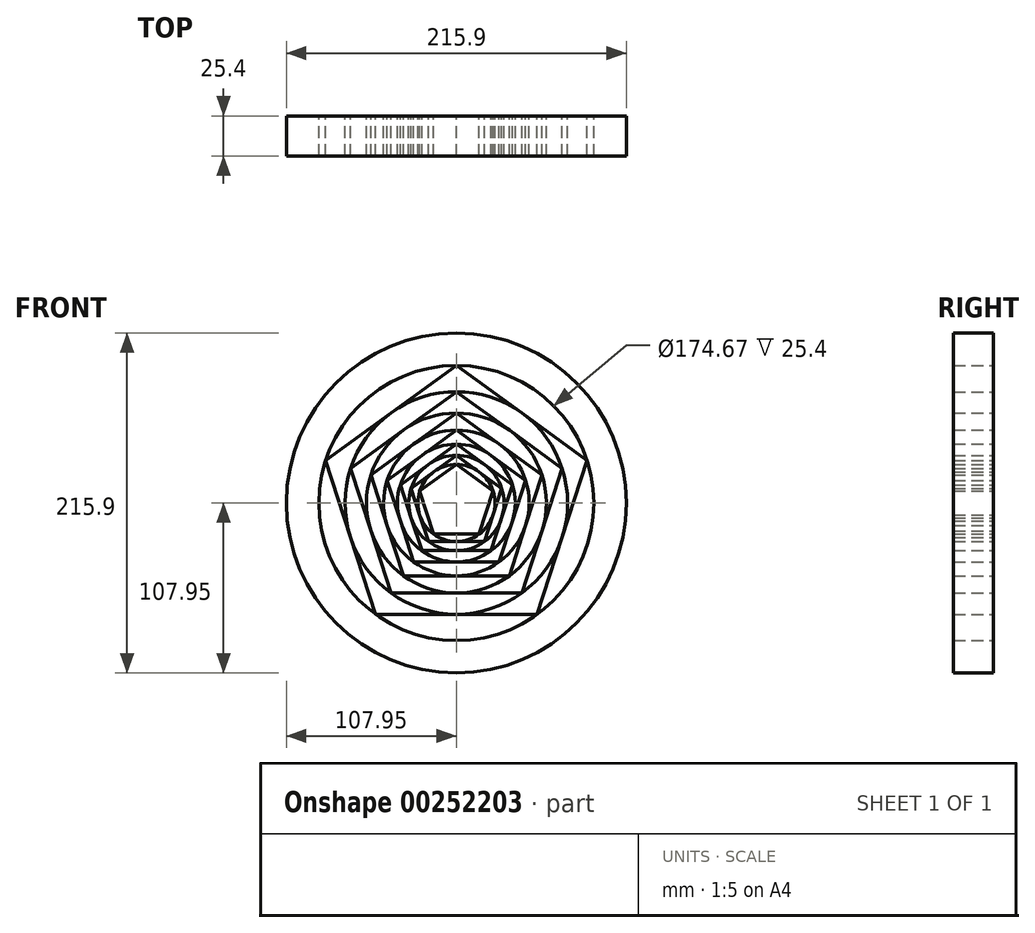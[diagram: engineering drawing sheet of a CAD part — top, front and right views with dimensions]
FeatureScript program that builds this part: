
annotation { "Feature Type Name" : "Feature", "Feature Type Description" : "" }
export const myFeature = defineFeature(function(context is Context, id is Id, definition is map)
    precondition{}
    {
        {
            var Q0;
            Q0=qCreatedBy(makeId("Front.planeOp"),FACE);
            var sketch = newSketch(context, id + "F0", { "sketchPlane" : qUnion([Q0])});
            skCircle(sketch, "E0", {"center": v(0, 0) * mm, "radius": 107.95 * mm});
            skCircle(sketch, "E1.cCircle", {"center": v(0, 0) * mm, "radius": 107.95 * mm, "construction": true});
            skLineSegment(sketch, "E2.0", {"start": v(-2.52, 107.92) * mm, "end": v(101.86, 35.74) * mm});
            skLineSegment(sketch, "E2.1", {"start": v(101.86, 35.74) * mm, "end": v(65.47, -85.83) * mm});
            skLineSegment(sketch, "E2.2", {"start": v(65.47, -85.83) * mm, "end": v(-61.4, -88.79) * mm});
            skLineSegment(sketch, "E2.3", {"start": v(-61.4, -88.79) * mm, "end": v(-103.42, 30.96) * mm});
            skLineSegment(sketch, "E2.4", {"start": v(-103.42, 30.96) * mm, "end": v(-2.52, 107.92) * mm});
            skCircle(sketch, "E3", {"center": v(0, 0) * mm, "radius": 87.33 * mm});
            skCircle(sketch, "E4.cCircle", {"center": v(0, 0) * mm, "radius": 87.33 * mm, "construction": true});
            skLineSegment(sketch, "E4.0", {"start": v(0, 87.33) * mm, "end": v(83.06, 26.99) * mm});
            skLineSegment(sketch, "E4.1", {"start": v(83.06, 26.99) * mm, "end": v(51.33, -70.65) * mm});
            skLineSegment(sketch, "E4.2", {"start": v(51.33, -70.65) * mm, "end": v(-51.33, -70.65) * mm});
            skLineSegment(sketch, "E4.3", {"start": v(-51.33, -70.65) * mm, "end": v(-83.06, 26.99) * mm});
            skLineSegment(sketch, "E4.4", {"start": v(-83.06, 26.99) * mm, "end": v(0, 87.33) * mm});
            skCircle(sketch, "E5", {"center": v(0, 0) * mm, "radius": 70.65 * mm});
            skCircle(sketch, "E6.cCircle", {"center": v(0, 0) * mm, "radius": 70.65 * mm, "construction": true});
            skLineSegment(sketch, "E6.0", {"start": v(0, 70.65) * mm, "end": v(67.2, 21.83) * mm});
            skLineSegment(sketch, "E6.1", {"start": v(67.2, 21.83) * mm, "end": v(41.53, -57.16) * mm});
            skLineSegment(sketch, "E6.2", {"start": v(41.53, -57.16) * mm, "end": v(-41.53, -57.16) * mm});
            skLineSegment(sketch, "E6.3", {"start": v(-41.53, -57.16) * mm, "end": v(-67.2, 21.83) * mm});
            skLineSegment(sketch, "E6.4", {"start": v(-67.2, 21.83) * mm, "end": v(0, 70.65) * mm});
            skCircle(sketch, "E7", {"center": v(0, 0) * mm, "radius": 57.16 * mm});
            skCircle(sketch, "E8.cCircle", {"center": v(0, 0) * mm, "radius": 57.16 * mm, "construction": true});
            skLineSegment(sketch, "E8.0", {"start": v(0, 57.16) * mm, "end": v(54.36, 17.66) * mm});
            skLineSegment(sketch, "E8.1", {"start": v(54.36, 17.66) * mm, "end": v(33.6, -46.24) * mm});
            skLineSegment(sketch, "E8.2", {"start": v(33.6, -46.24) * mm, "end": v(-33.6, -46.24) * mm});
            skLineSegment(sketch, "E8.3", {"start": v(-33.6, -46.24) * mm, "end": v(-54.36, 17.66) * mm});
            skLineSegment(sketch, "E8.4", {"start": v(-54.36, 17.66) * mm, "end": v(0, 57.16) * mm});
            skCircle(sketch, "E9", {"center": v(0, 0) * mm, "radius": 46.24 * mm});
            skCircle(sketch, "E10.cCircle", {"center": v(0, 0) * mm, "radius": 46.24 * mm, "construction": true});
            skLineSegment(sketch, "E10.0", {"start": v(0, 46.24) * mm, "end": v(43.98, 14.3) * mm});
            skLineSegment(sketch, "E10.1", {"start": v(43.98, 14.3) * mm, "end": v(27.18, -37.41) * mm});
            skLineSegment(sketch, "E10.2", {"start": v(27.18, -37.41) * mm, "end": v(-27.18, -37.41) * mm});
            skLineSegment(sketch, "E10.3", {"start": v(-27.18, -37.41) * mm, "end": v(-43.98, 14.3) * mm});
            skLineSegment(sketch, "E10.4", {"start": v(-43.98, 14.3) * mm, "end": v(0, 46.24) * mm});
            skCircle(sketch, "E11", {"center": v(0, 0) * mm, "radius": 37.41 * mm});
            skCircle(sketch, "E12.cCircle", {"center": v(0, 0) * mm, "radius": 37.41 * mm, "construction": true});
            skLineSegment(sketch, "E12.0", {"start": v(0, 37.41) * mm, "end": v(35.58, 11.56) * mm});
            skLineSegment(sketch, "E12.1", {"start": v(35.58, 11.56) * mm, "end": v(22, -30.27) * mm});
            skLineSegment(sketch, "E12.2", {"start": v(22, -30.27) * mm, "end": v(-22, -30.27) * mm});
            skLineSegment(sketch, "E12.3", {"start": v(-22, -30.27) * mm, "end": v(-35.58, 11.56) * mm});
            skLineSegment(sketch, "E12.4", {"start": v(-35.58, 11.56) * mm, "end": v(0, 37.41) * mm});
            skCircle(sketch, "E13", {"center": v(0, 0) * mm, "radius": 30.27 * mm});
            skCircle(sketch, "E14.cCircle", {"center": v(0, 0) * mm, "radius": 30.27 * mm, "construction": true});
            skLineSegment(sketch, "E14.0", {"start": v(0, 30.27) * mm, "end": v(28.79, 9.35) * mm});
            skLineSegment(sketch, "E14.1", {"start": v(28.79, 9.35) * mm, "end": v(17.8, -24.49) * mm});
            skLineSegment(sketch, "E14.2", {"start": v(17.8, -24.49) * mm, "end": v(-17.8, -24.49) * mm});
            skLineSegment(sketch, "E14.3", {"start": v(-17.8, -24.49) * mm, "end": v(-28.79, 9.35) * mm});
            skLineSegment(sketch, "E14.4", {"start": v(-28.79, 9.35) * mm, "end": v(0, 30.27) * mm});
            skCircle(sketch, "E15", {"center": v(0, 0) * mm, "radius": 24.49 * mm});
            skCircle(sketch, "E16.cCircle", {"center": v(0, 0) * mm, "radius": 24.49 * mm, "construction": true});
            skLineSegment(sketch, "E16.0", {"start": v(0, 24.49) * mm, "end": v(23.29, 7.57) * mm});
            skLineSegment(sketch, "E16.1", {"start": v(23.29, 7.57) * mm, "end": v(14.4, -19.8) * mm});
            skLineSegment(sketch, "E16.2", {"start": v(14.4, -19.8) * mm, "end": v(-14.4, -19.8) * mm});
            skLineSegment(sketch, "E16.3", {"start": v(-14.4, -19.8) * mm, "end": v(-23.29, 7.57) * mm});
            skLineSegment(sketch, "E16.4", {"start": v(-23.29, 7.57) * mm, "end": v(0, 24.49) * mm});
            skSolve(sketch);
        }
        {
            var Q0;
            Q0 = qSketchRegion(id + "F0", true);
            var Q1;
            Q1=makeQuery(id+"F0.imprint","IMPRINT",FACE,{"disambiguationData":[TD([[makeQuery(id+"F0.imprint","IMPRINT",EDGE,{"derivedFrom":sQuery(id+"F0.wireOp",EDGE,"E16.0")}),-1.0]])]});
            var Q2;
            {var subQ1=sQuery(id+"F0.wireOp",EDGE,"E14.3");var subQ3=sQuery(id+"F0.wireOp",EDGE,"E15");var subQ4=makeQuery(id+"F0.imprint","INTERSECT",VERTEX,{"derivedFrom":[subQ1,subQ3]});Q2=makeQuery(id+"F0.imprint","IMPRINT",FACE,{"disambiguationData":[TD([[makeQuery(id+"F0.imprint","IMPRINT",EDGE,{"disambiguationData":[TD([[subQ4,-1.0]])],"derivedFrom":subQ1}),-1.0]])]});}
            var Q3;
            {var subQ1=sQuery(id+"F0.wireOp",EDGE,"E14.2");var subQ3=sQuery(id+"F0.wireOp",EDGE,"E15");var subQ4=makeQuery(id+"F0.imprint","INTERSECT",VERTEX,{"derivedFrom":[subQ1,subQ3]});Q3=makeQuery(id+"F0.imprint","IMPRINT",FACE,{"disambiguationData":[TD([[makeQuery(id+"F0.imprint","IMPRINT",EDGE,{"disambiguationData":[TD([[subQ4,-1.0]])],"derivedFrom":subQ1}),-1.0]])]});}
            var Q4;
            {var subQ1=sQuery(id+"F0.wireOp",EDGE,"E14.1");var subQ3=sQuery(id+"F0.wireOp",EDGE,"E15");var subQ4=makeQuery(id+"F0.imprint","INTERSECT",VERTEX,{"derivedFrom":[subQ1,subQ3]});Q4=makeQuery(id+"F0.imprint","IMPRINT",FACE,{"disambiguationData":[TD([[makeQuery(id+"F0.imprint","IMPRINT",EDGE,{"disambiguationData":[TD([[subQ4,-1.0]])],"derivedFrom":subQ1}),-1.0]])]});}
            var Q5;
            {var subQ1=sQuery(id+"F0.wireOp",EDGE,"E14.0");var subQ3=sQuery(id+"F0.wireOp",EDGE,"E15");var subQ4=makeQuery(id+"F0.imprint","INTERSECT",VERTEX,{"derivedFrom":[subQ1,subQ3]});Q5=makeQuery(id+"F0.imprint","IMPRINT",FACE,{"disambiguationData":[TD([[makeQuery(id+"F0.imprint","IMPRINT",EDGE,{"disambiguationData":[TD([[subQ4,-1.0]])],"derivedFrom":subQ1}),-1.0]])]});}
            var Q6;
            {var subQ1=sQuery(id+"F0.wireOp",EDGE,"E14.0");var subQ3=sQuery(id+"F0.wireOp",EDGE,"E15");var subQ4=makeQuery(id+"F0.imprint","INTERSECT",VERTEX,{"derivedFrom":[subQ1,subQ3]});Q6=makeQuery(id+"F0.imprint","IMPRINT",FACE,{"disambiguationData":[TD([[makeQuery(id+"F0.imprint","IMPRINT",EDGE,{"disambiguationData":[TD([[subQ4,1.0]])],"derivedFrom":subQ1}),-1.0]])]});}
            var Q7;
            {var subQ1=sQuery(id+"F0.wireOp",EDGE,"E12.0");var subQ3=sQuery(id+"F0.wireOp",EDGE,"E13");var subQ4=makeQuery(id+"F0.imprint","INTERSECT",VERTEX,{"derivedFrom":[subQ1,subQ3]});Q7=makeQuery(id+"F0.imprint","IMPRINT",FACE,{"disambiguationData":[TD([[makeQuery(id+"F0.imprint","IMPRINT",EDGE,{"disambiguationData":[TD([[subQ4,1.0]])],"derivedFrom":subQ1}),-1.0]])]});}
            var Q8;
            {var subQ1=sQuery(id+"F0.wireOp",EDGE,"E12.3");var subQ3=sQuery(id+"F0.wireOp",EDGE,"E13");var subQ4=makeQuery(id+"F0.imprint","INTERSECT",VERTEX,{"derivedFrom":[subQ1,subQ3]});Q8=makeQuery(id+"F0.imprint","IMPRINT",FACE,{"disambiguationData":[TD([[makeQuery(id+"F0.imprint","IMPRINT",EDGE,{"disambiguationData":[TD([[subQ4,-1.0]])],"derivedFrom":subQ1}),-1.0]])]});}
            var Q9;
            {var subQ1=sQuery(id+"F0.wireOp",EDGE,"E12.2");var subQ3=sQuery(id+"F0.wireOp",EDGE,"E13");var subQ4=makeQuery(id+"F0.imprint","INTERSECT",VERTEX,{"derivedFrom":[subQ1,subQ3]});Q9=makeQuery(id+"F0.imprint","IMPRINT",FACE,{"disambiguationData":[TD([[makeQuery(id+"F0.imprint","IMPRINT",EDGE,{"disambiguationData":[TD([[subQ4,-1.0]])],"derivedFrom":subQ1}),-1.0]])]});}
            var Q10;
            {var subQ1=sQuery(id+"F0.wireOp",EDGE,"E12.1");var subQ3=sQuery(id+"F0.wireOp",EDGE,"E13");var subQ4=makeQuery(id+"F0.imprint","INTERSECT",VERTEX,{"derivedFrom":[subQ1,subQ3]});Q10=makeQuery(id+"F0.imprint","IMPRINT",FACE,{"disambiguationData":[TD([[makeQuery(id+"F0.imprint","IMPRINT",EDGE,{"disambiguationData":[TD([[subQ4,-1.0]])],"derivedFrom":subQ1}),-1.0]])]});}
            var Q11;
            {var subQ1=sQuery(id+"F0.wireOp",EDGE,"E12.0");var subQ3=sQuery(id+"F0.wireOp",EDGE,"E13");var subQ4=makeQuery(id+"F0.imprint","INTERSECT",VERTEX,{"derivedFrom":[subQ1,subQ3]});Q11=makeQuery(id+"F0.imprint","IMPRINT",FACE,{"disambiguationData":[TD([[makeQuery(id+"F0.imprint","IMPRINT",EDGE,{"disambiguationData":[TD([[subQ4,-1.0]])],"derivedFrom":subQ1}),-1.0]])]});}
            var Q12;
            {var subQ1=sQuery(id+"F0.wireOp",EDGE,"E10.0");var subQ3=sQuery(id+"F0.wireOp",EDGE,"E11");var subQ4=makeQuery(id+"F0.imprint","INTERSECT",VERTEX,{"derivedFrom":[subQ1,subQ3]});Q12=makeQuery(id+"F0.imprint","IMPRINT",FACE,{"disambiguationData":[TD([[makeQuery(id+"F0.imprint","IMPRINT",EDGE,{"disambiguationData":[TD([[subQ4,1.0]])],"derivedFrom":subQ1}),-1.0]])]});}
            var Q13;
            {var subQ1=sQuery(id+"F0.wireOp",EDGE,"E10.3");var subQ3=sQuery(id+"F0.wireOp",EDGE,"E11");var subQ4=makeQuery(id+"F0.imprint","INTERSECT",VERTEX,{"derivedFrom":[subQ1,subQ3]});Q13=makeQuery(id+"F0.imprint","IMPRINT",FACE,{"disambiguationData":[TD([[makeQuery(id+"F0.imprint","IMPRINT",EDGE,{"disambiguationData":[TD([[subQ4,-1.0]])],"derivedFrom":subQ1}),-1.0]])]});}
            var Q14;
            {var subQ1=sQuery(id+"F0.wireOp",EDGE,"E10.2");var subQ3=sQuery(id+"F0.wireOp",EDGE,"E11");var subQ4=makeQuery(id+"F0.imprint","INTERSECT",VERTEX,{"derivedFrom":[subQ1,subQ3]});Q14=makeQuery(id+"F0.imprint","IMPRINT",FACE,{"disambiguationData":[TD([[makeQuery(id+"F0.imprint","IMPRINT",EDGE,{"disambiguationData":[TD([[subQ4,-1.0]])],"derivedFrom":subQ1}),-1.0]])]});}
            var Q15;
            {var subQ1=sQuery(id+"F0.wireOp",EDGE,"E10.1");var subQ3=sQuery(id+"F0.wireOp",EDGE,"E11");var subQ4=makeQuery(id+"F0.imprint","INTERSECT",VERTEX,{"derivedFrom":[subQ1,subQ3]});Q15=makeQuery(id+"F0.imprint","IMPRINT",FACE,{"disambiguationData":[TD([[makeQuery(id+"F0.imprint","IMPRINT",EDGE,{"disambiguationData":[TD([[subQ4,-1.0]])],"derivedFrom":subQ1}),-1.0]])]});}
            var Q16;
            {var subQ1=sQuery(id+"F0.wireOp",EDGE,"E10.0");var subQ3=sQuery(id+"F0.wireOp",EDGE,"E11");var subQ4=makeQuery(id+"F0.imprint","INTERSECT",VERTEX,{"derivedFrom":[subQ1,subQ3]});Q16=makeQuery(id+"F0.imprint","IMPRINT",FACE,{"disambiguationData":[TD([[makeQuery(id+"F0.imprint","IMPRINT",EDGE,{"disambiguationData":[TD([[subQ4,-1.0]])],"derivedFrom":subQ1}),-1.0]])]});}
            var Q17;
            {var subQ1=sQuery(id+"F0.wireOp",EDGE,"E8.0");var subQ3=sQuery(id+"F0.wireOp",EDGE,"E9");var subQ4=makeQuery(id+"F0.imprint","INTERSECT",VERTEX,{"derivedFrom":[subQ1,subQ3]});Q17=makeQuery(id+"F0.imprint","IMPRINT",FACE,{"disambiguationData":[TD([[makeQuery(id+"F0.imprint","IMPRINT",EDGE,{"disambiguationData":[TD([[subQ4,1.0]])],"derivedFrom":subQ1}),-1.0]])]});}
            var Q18;
            {var subQ1=sQuery(id+"F0.wireOp",EDGE,"E8.3");var subQ3=sQuery(id+"F0.wireOp",EDGE,"E9");var subQ4=makeQuery(id+"F0.imprint","INTERSECT",VERTEX,{"derivedFrom":[subQ1,subQ3]});Q18=makeQuery(id+"F0.imprint","IMPRINT",FACE,{"disambiguationData":[TD([[makeQuery(id+"F0.imprint","IMPRINT",EDGE,{"disambiguationData":[TD([[subQ4,-1.0]])],"derivedFrom":subQ1}),-1.0]])]});}
            var Q19;
            {var subQ1=sQuery(id+"F0.wireOp",EDGE,"E8.2");var subQ3=sQuery(id+"F0.wireOp",EDGE,"E9");var subQ4=makeQuery(id+"F0.imprint","INTERSECT",VERTEX,{"derivedFrom":[subQ1,subQ3]});Q19=makeQuery(id+"F0.imprint","IMPRINT",FACE,{"disambiguationData":[TD([[makeQuery(id+"F0.imprint","IMPRINT",EDGE,{"disambiguationData":[TD([[subQ4,-1.0]])],"derivedFrom":subQ1}),-1.0]])]});}
            var Q20;
            {var subQ1=sQuery(id+"F0.wireOp",EDGE,"E8.1");var subQ3=sQuery(id+"F0.wireOp",EDGE,"E9");var subQ4=makeQuery(id+"F0.imprint","INTERSECT",VERTEX,{"derivedFrom":[subQ1,subQ3]});Q20=makeQuery(id+"F0.imprint","IMPRINT",FACE,{"disambiguationData":[TD([[makeQuery(id+"F0.imprint","IMPRINT",EDGE,{"disambiguationData":[TD([[subQ4,-1.0]])],"derivedFrom":subQ1}),-1.0]])]});}
            var Q21;
            {var subQ1=sQuery(id+"F0.wireOp",EDGE,"E8.0");var subQ3=sQuery(id+"F0.wireOp",EDGE,"E9");var subQ4=makeQuery(id+"F0.imprint","INTERSECT",VERTEX,{"derivedFrom":[subQ1,subQ3]});Q21=makeQuery(id+"F0.imprint","IMPRINT",FACE,{"disambiguationData":[TD([[makeQuery(id+"F0.imprint","IMPRINT",EDGE,{"disambiguationData":[TD([[subQ4,-1.0]])],"derivedFrom":subQ1}),-1.0]])]});}
            var Q22;
            {var subQ1=sQuery(id+"F0.wireOp",EDGE,"E6.0");var subQ3=sQuery(id+"F0.wireOp",EDGE,"E7");var subQ4=makeQuery(id+"F0.imprint","INTERSECT",VERTEX,{"derivedFrom":[subQ1,subQ3]});Q22=makeQuery(id+"F0.imprint","IMPRINT",FACE,{"disambiguationData":[TD([[makeQuery(id+"F0.imprint","IMPRINT",EDGE,{"disambiguationData":[TD([[subQ4,1.0]])],"derivedFrom":subQ1}),-1.0]])]});}
            var Q23;
            {var subQ1=sQuery(id+"F0.wireOp",EDGE,"E6.3");var subQ3=sQuery(id+"F0.wireOp",EDGE,"E7");var subQ4=makeQuery(id+"F0.imprint","INTERSECT",VERTEX,{"derivedFrom":[subQ1,subQ3]});Q23=makeQuery(id+"F0.imprint","IMPRINT",FACE,{"disambiguationData":[TD([[makeQuery(id+"F0.imprint","IMPRINT",EDGE,{"disambiguationData":[TD([[subQ4,-1.0]])],"derivedFrom":subQ1}),-1.0]])]});}
            var Q24;
            {var subQ1=sQuery(id+"F0.wireOp",EDGE,"E6.2");var subQ3=sQuery(id+"F0.wireOp",EDGE,"E7");var subQ4=makeQuery(id+"F0.imprint","INTERSECT",VERTEX,{"derivedFrom":[subQ1,subQ3]});Q24=makeQuery(id+"F0.imprint","IMPRINT",FACE,{"disambiguationData":[TD([[makeQuery(id+"F0.imprint","IMPRINT",EDGE,{"disambiguationData":[TD([[subQ4,-1.0]])],"derivedFrom":subQ1}),-1.0]])]});}
            var Q25;
            {var subQ1=sQuery(id+"F0.wireOp",EDGE,"E6.1");var subQ3=sQuery(id+"F0.wireOp",EDGE,"E7");var subQ4=makeQuery(id+"F0.imprint","INTERSECT",VERTEX,{"derivedFrom":[subQ1,subQ3]});Q25=makeQuery(id+"F0.imprint","IMPRINT",FACE,{"disambiguationData":[TD([[makeQuery(id+"F0.imprint","IMPRINT",EDGE,{"disambiguationData":[TD([[subQ4,-1.0]])],"derivedFrom":subQ1}),-1.0]])]});}
            var Q26;
            {var subQ1=sQuery(id+"F0.wireOp",EDGE,"E6.0");var subQ3=sQuery(id+"F0.wireOp",EDGE,"E7");var subQ4=makeQuery(id+"F0.imprint","INTERSECT",VERTEX,{"derivedFrom":[subQ1,subQ3]});Q26=makeQuery(id+"F0.imprint","IMPRINT",FACE,{"disambiguationData":[TD([[makeQuery(id+"F0.imprint","IMPRINT",EDGE,{"disambiguationData":[TD([[subQ4,-1.0]])],"derivedFrom":subQ1}),-1.0]])]});}
            var Q27;
            {var subQ1=sQuery(id+"F0.wireOp",EDGE,"E4.0");var subQ3=sQuery(id+"F0.wireOp",EDGE,"E5");var subQ4=makeQuery(id+"F0.imprint","INTERSECT",VERTEX,{"derivedFrom":[subQ1,subQ3]});Q27=makeQuery(id+"F0.imprint","IMPRINT",FACE,{"disambiguationData":[TD([[makeQuery(id+"F0.imprint","IMPRINT",EDGE,{"disambiguationData":[TD([[subQ4,1.0]])],"derivedFrom":subQ1}),-1.0]])]});}
            var Q28;
            {var subQ1=sQuery(id+"F0.wireOp",EDGE,"E4.3");var subQ3=sQuery(id+"F0.wireOp",EDGE,"E5");var subQ4=makeQuery(id+"F0.imprint","INTERSECT",VERTEX,{"derivedFrom":[subQ1,subQ3]});Q28=makeQuery(id+"F0.imprint","IMPRINT",FACE,{"disambiguationData":[TD([[makeQuery(id+"F0.imprint","IMPRINT",EDGE,{"disambiguationData":[TD([[subQ4,-1.0]])],"derivedFrom":subQ1}),-1.0]])]});}
            var Q29;
            {var subQ1=sQuery(id+"F0.wireOp",EDGE,"E4.2");var subQ3=sQuery(id+"F0.wireOp",EDGE,"E5");var subQ4=makeQuery(id+"F0.imprint","INTERSECT",VERTEX,{"derivedFrom":[subQ1,subQ3]});Q29=makeQuery(id+"F0.imprint","IMPRINT",FACE,{"disambiguationData":[TD([[makeQuery(id+"F0.imprint","IMPRINT",EDGE,{"disambiguationData":[TD([[subQ4,-1.0]])],"derivedFrom":subQ1}),-1.0]])]});}
            var Q30;
            {var subQ1=sQuery(id+"F0.wireOp",EDGE,"E4.1");var subQ3=sQuery(id+"F0.wireOp",EDGE,"E5");var subQ4=makeQuery(id+"F0.imprint","INTERSECT",VERTEX,{"derivedFrom":[subQ1,subQ3]});Q30=makeQuery(id+"F0.imprint","IMPRINT",FACE,{"disambiguationData":[TD([[makeQuery(id+"F0.imprint","IMPRINT",EDGE,{"disambiguationData":[TD([[subQ4,-1.0]])],"derivedFrom":subQ1}),-1.0]])]});}
            var Q31;
            {var subQ1=sQuery(id+"F0.wireOp",EDGE,"E4.0");var subQ3=sQuery(id+"F0.wireOp",EDGE,"E5");var subQ4=makeQuery(id+"F0.imprint","INTERSECT",VERTEX,{"derivedFrom":[subQ1,subQ3]});Q31=makeQuery(id+"F0.imprint","IMPRINT",FACE,{"disambiguationData":[TD([[makeQuery(id+"F0.imprint","IMPRINT",EDGE,{"disambiguationData":[TD([[subQ4,-1.0]])],"derivedFrom":subQ1}),-1.0]])]});}
            extrude(context, id + "F1", {"entities" : qUnion([Q0, Q1, Q2, Q3, Q4, Q5, Q6, Q7, Q8, Q9, Q10, Q11, Q12, Q13, Q14, Q15, Q16, Q17, Q18, Q19, Q20, Q21, Q22, Q23, Q24, Q25, Q26, Q27, Q28, Q29, Q30, Q31]), "depth" : 25.4 * mm});
        }
    });
